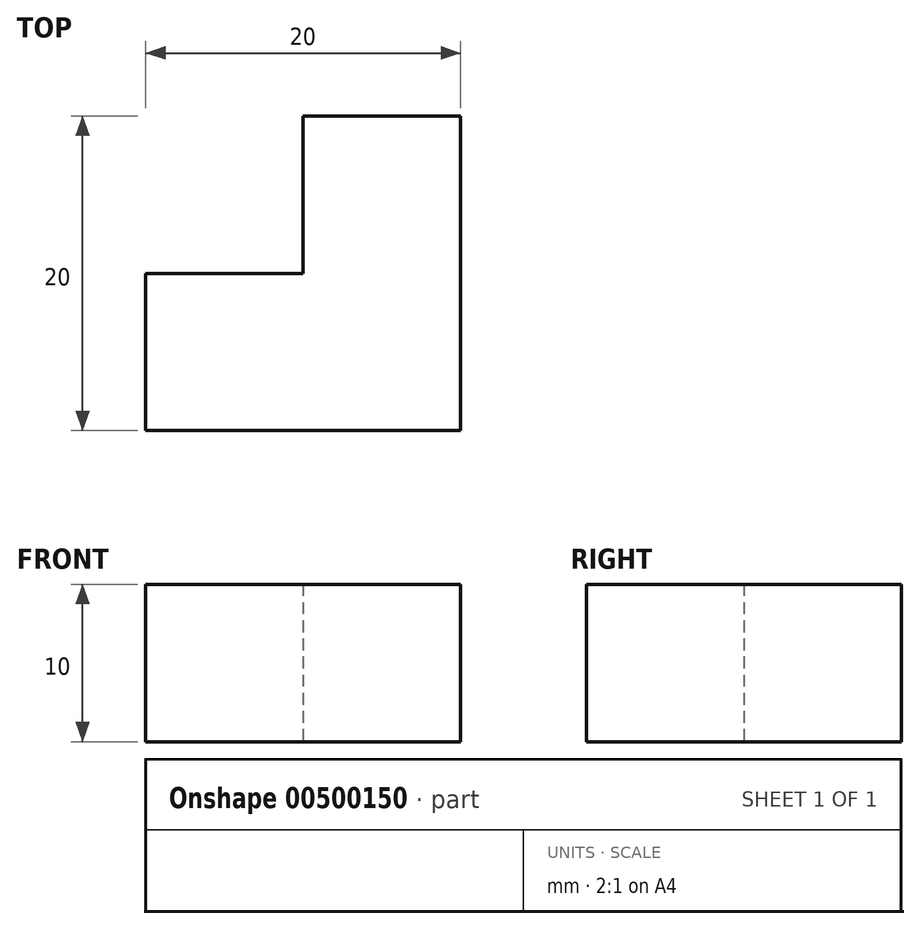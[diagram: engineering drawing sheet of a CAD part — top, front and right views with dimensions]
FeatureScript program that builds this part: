
annotation { "Feature Type Name" : "Feature", "Feature Type Description" : "" }
export const myFeature = defineFeature(function(context is Context, id is Id, definition is map)
    precondition{}
    {
        {
            var Q0;
            Q0=qCreatedBy(makeId("Top.planeOp"),FACE);
            var sketch = newSketch(context, id + "F0", { "sketchPlane" : qUnion([Q0])});
            skLineSegment(sketch, "E0", {"start": v(0, 0) * mm, "end": v(0, 10) * mm});
            skLineSegment(sketch, "E1", {"start": v(0, 10) * mm, "end": v(10, 10) * mm});
            skLineSegment(sketch, "E2", {"start": v(10, 10) * mm, "end": v(10, 20) * mm});
            skLineSegment(sketch, "E3", {"start": v(10, 20) * mm, "end": v(20, 20) * mm});
            skLineSegment(sketch, "E4", {"start": v(20, 20) * mm, "end": v(20, 0) * mm});
            skLineSegment(sketch, "E5", {"start": v(0, 0) * mm, "end": v(20, 0) * mm});
            skSolve(sketch);
        }
        {
            var Q0;
            Q0=makeQuery(id+"F0.imprint","IMPRINT",FACE,{"disambiguationData":[TD([[makeQuery(id+"F0.imprint","IMPRINT",EDGE,{"derivedFrom":sQuery(id+"F0.wireOp",EDGE,"E0")}),-1.0]])]});
            var sketch = newSketch(context, id + "F1", { "sketchPlane" : qUnion([Q0])});
            skSolve(sketch);
        }
        {
            var Q0;
            Q0=qSketchRegion(id+"F1",true);
            var Q1;
            Q1=makeQuery(id+"F0.imprint","IMPRINT",FACE,{"disambiguationData":[TD([[makeQuery(id+"F0.imprint","IMPRINT",EDGE,{"derivedFrom":sQuery(id+"F0.wireOp",EDGE,"E0")}),-1.0]])]});
            extrude(context, id + "F2", {"entities" : qUnion([Q0, Q1]), "depth" : 10 * mm});
        }
    });
